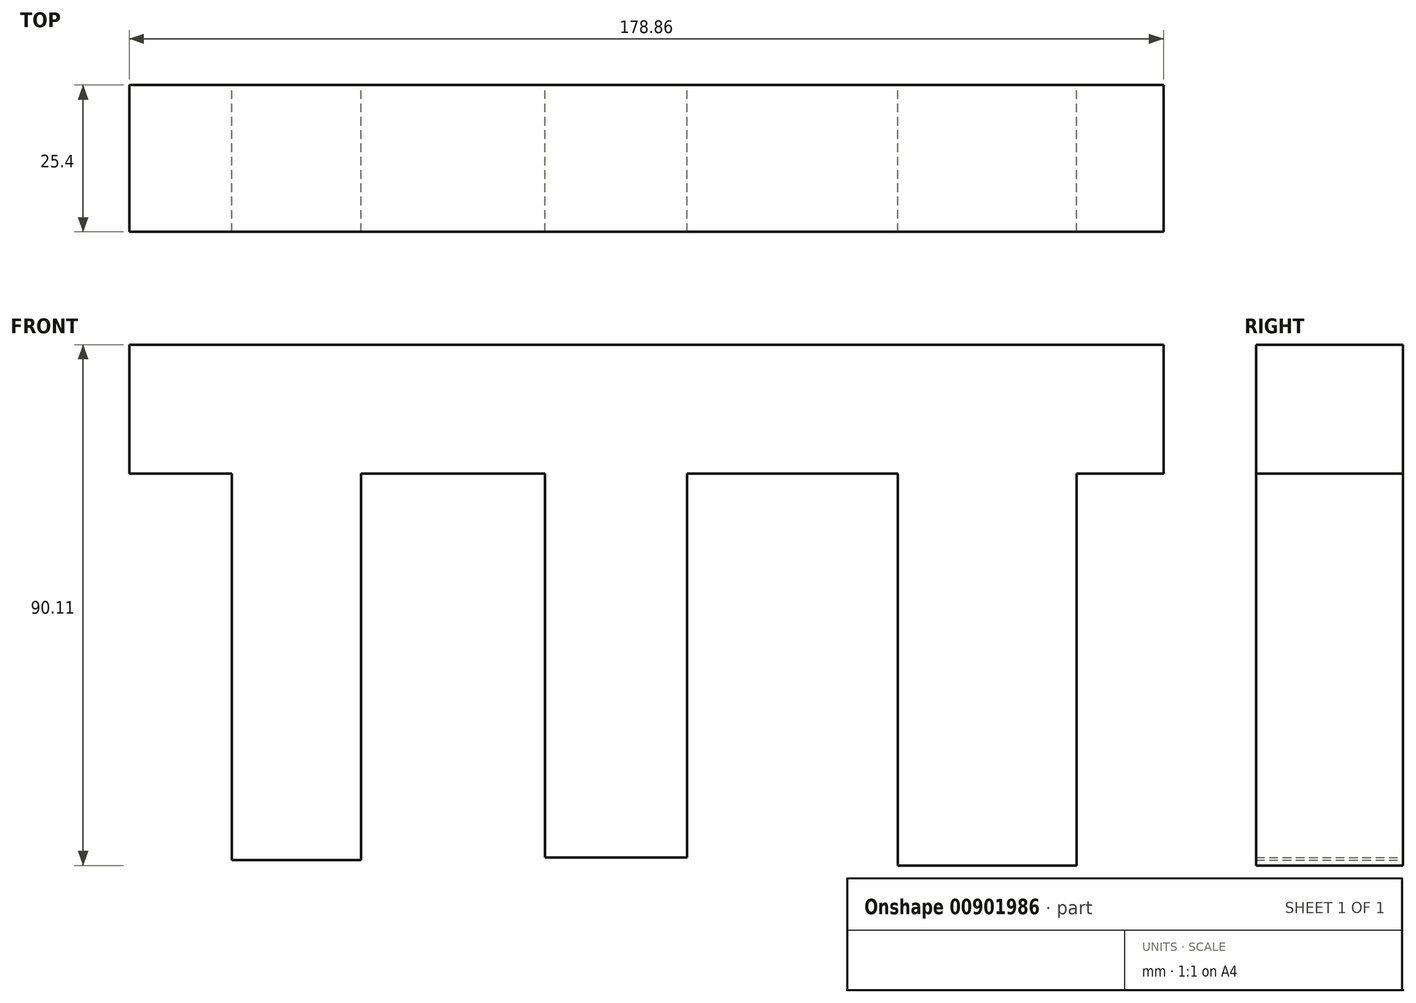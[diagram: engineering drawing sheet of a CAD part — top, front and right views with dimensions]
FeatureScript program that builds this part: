
annotation { "Feature Type Name" : "Feature", "Feature Type Description" : "" }
export const myFeature = defineFeature(function(context is Context, id is Id, definition is map)
    precondition{}
    {
        {
            var Q0;
            Q0=qCreatedBy(makeId("Front.planeOp"),FACE);
            var sketch = newSketch(context, id + "F0", { "sketchPlane" : qUnion([Q0])});
            skLineSegment(sketch, "E0.bottom", {"start": v(89.43, -11.15) * mm, "end": v(-89.43, -11.15) * mm});
            skLineSegment(sketch, "E0.top", {"start": v(89.43, 11.15) * mm, "end": v(-89.43, 11.15) * mm});
            skLineSegment(sketch, "E0.left", {"start": v(89.43, -11.15) * mm, "end": v(89.43, 11.15) * mm});
            skLineSegment(sketch, "E0.right", {"start": v(-89.43, -11.15) * mm, "end": v(-89.43, 11.15) * mm});
            skPoint(sketch, "E0.middle", {"position": v(0, 0) * mm});
            skLineSegment(sketch, "E1", {"start": v(-71.68, -11.15) * mm, "end": v(-71.68, -78.05) * mm});
            skLineSegment(sketch, "E2", {"start": v(-71.68, -78.05) * mm, "end": v(-49.38, -78.05) * mm});
            skLineSegment(sketch, "E3", {"start": v(-49.38, -78.05) * mm, "end": v(-49.38, -11.15) * mm});
            skLineSegment(sketch, "E4", {"start": v(-17.52, -11.15) * mm, "end": v(-17.52, -77.6) * mm});
            skLineSegment(sketch, "E5", {"start": v(-17.52, -77.6) * mm, "end": v(7.05, -77.6) * mm});
            skLineSegment(sketch, "E6", {"start": v(7.05, -77.6) * mm, "end": v(7.05, -11.15) * mm});
            skLineSegment(sketch, "E7", {"start": v(43.46, -11.15) * mm, "end": v(43.46, -78.96) * mm});
            skLineSegment(sketch, "E8", {"start": v(43.46, -78.96) * mm, "end": v(74.4, -78.96) * mm});
            skLineSegment(sketch, "E9", {"start": v(74.4, -78.96) * mm, "end": v(74.4, -11.15) * mm});
            skSolve(sketch);
        }
        {
            var Q0;
            Q0=makeQuery(id+"F0.imprint","IMPRINT",FACE,{"disambiguationData":[TD([[makeQuery(id+"F0.imprint","IMPRINT",EDGE,{"derivedFrom":sQuery(id+"F0.wireOp",EDGE,"E0.top")}),1.0]])]});
            var Q1;
            {var subQ0=sQuery(id+"F0.wireOp",EDGE,"E1");Q1=makeQuery(id+"F0.imprint","IMPRINT",FACE,{"disambiguationData":[TD([[makeQuery(id+"F0.imprint","IMPRINT",EDGE,{"derivedFrom":subQ0}),1.0]])]});}
            var Q2;
            {var subQ0=sQuery(id+"F0.wireOp",EDGE,"E4");Q2=makeQuery(id+"F0.imprint","IMPRINT",FACE,{"disambiguationData":[TD([[makeQuery(id+"F0.imprint","IMPRINT",EDGE,{"derivedFrom":subQ0}),1.0]])]});}
            var Q3;
            {var subQ0=sQuery(id+"F0.wireOp",EDGE,"E7");Q3=makeQuery(id+"F0.imprint","IMPRINT",FACE,{"disambiguationData":[TD([[makeQuery(id+"F0.imprint","IMPRINT",EDGE,{"derivedFrom":subQ0}),1.0]])]});}
            extrude(context, id + "F1", {"entities" : qUnion([Q0, Q1, Q2, Q3]), "depth" : 25.4 * mm, "offsetDistance" : 25.4 * mm});
        }
    });
